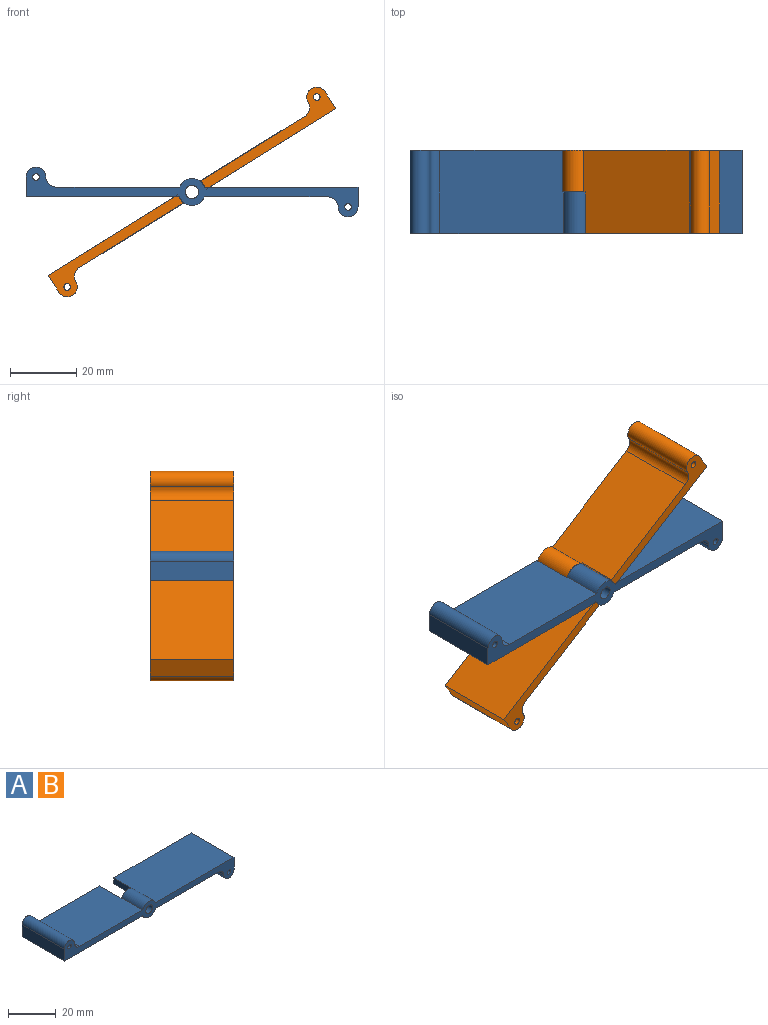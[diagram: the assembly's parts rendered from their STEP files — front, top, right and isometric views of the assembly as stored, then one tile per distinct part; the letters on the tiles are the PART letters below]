
ASSEMBLY  parts=2 mates=1
PART A: 21 faces, bbox 100x25x15 mm
  f0: plane 45.88x9mm, normal (0,1,0), area 168.6mm2, adj f8,f9,f10,f11,f13,f15,f19
  f1: cylinder r=4mm len=12.5mm, axis (0,1,0), area 118.6mm2, adj f2,f15,f16,f18
  f2: plane 37.29x25mm, normal (0,0,-1), area 927.1mm2, adj f1,f3,f16,f17,f18,f20
  f3: cylinder r=3mm len=25mm, axis (0,1,0), area 117.8mm2, adj f2,f4,f16,f17
  f4: cylinder r=3mm len=25mm, axis (0,1,0), area 235.6mm2, adj f3,f5,f16,f17
  f5: plane 25x6mm, normal (1,0,0), area 150mm2, adj f4,f6,f16,f17
  f6: plane 46.29x25mm, normal (0,0,1), area 1152.1mm2, adj f5,f7,f16,f17,f18,f20
  f7: cylinder r=4mm len=12.5mm, axis (0,1,0), area 118.6mm2, adj f6,f8,f16,f18
  f8: plane 37.29x25mm, normal (0,0,1), area 927.1mm2, adj f0,f7,f9,f16,f18,f19
  f9: cylinder r=3mm len=25mm, axis (0,1,0), area 117.8mm2, adj f0,f8,f10,f16
  f10: cylinder r=3mm len=25mm, axis (0,1,0), area 235.6mm2, adj f0,f9,f11,f16
  f11: plane 25x6mm, normal (-1,0,0), area 150mm2, adj f0,f10,f15,f16
  f12: cylinder r=2mm len=12.5mm, axis (0,1,0), area 157.1mm2, adj f16,f18
  f13: cylinder r=1mm len=25mm, axis (0,1,0), area 157.1mm2, adj f0,f16
  f14: cylinder r=1mm len=25mm, axis (0,1,0), area 157.1mm2, adj f16,f17
  f15: plane 46.29x25mm, normal (0,0,-1), area 1152.1mm2, adj f0,f1,f11,f16,f18,f19
  f16: plane 100x15mm, normal (0,-1,0), area 376.1mm2, adj f1,f2,f3,f4,f5,f6,f7,f8
  f17: plane 45.88x9mm, normal (0,1,0), area 168.6mm2, adj f2,f3,f4,f5,f6,f14,f20
  f18: plane 8.25x8mm, normal (0,1,0), area 39mm2, adj f1,f2,f6,f7,f8,f12,f15,f19
  f19: plane 12.5x3mm, normal (1,0,0), area 37.5mm2, adj f0,f8,f15,f18
  f20: plane 12.5x3mm, normal (-1,0,0), area 37.5mm2, adj f2,f6,f17,f18
PART B: same geometry as A
PLACE A t=(-13.12,-0.78,-8.56)mm fixed
PLACE B rot(axis=(0.27,0,-0.96),180deg) t=(-13.12,-25.78,-8.56)mm
MATE revolute A.f1 <-> B.f1  axis (0,1,0) through (-13.12,-13.28,-8.56)mm
